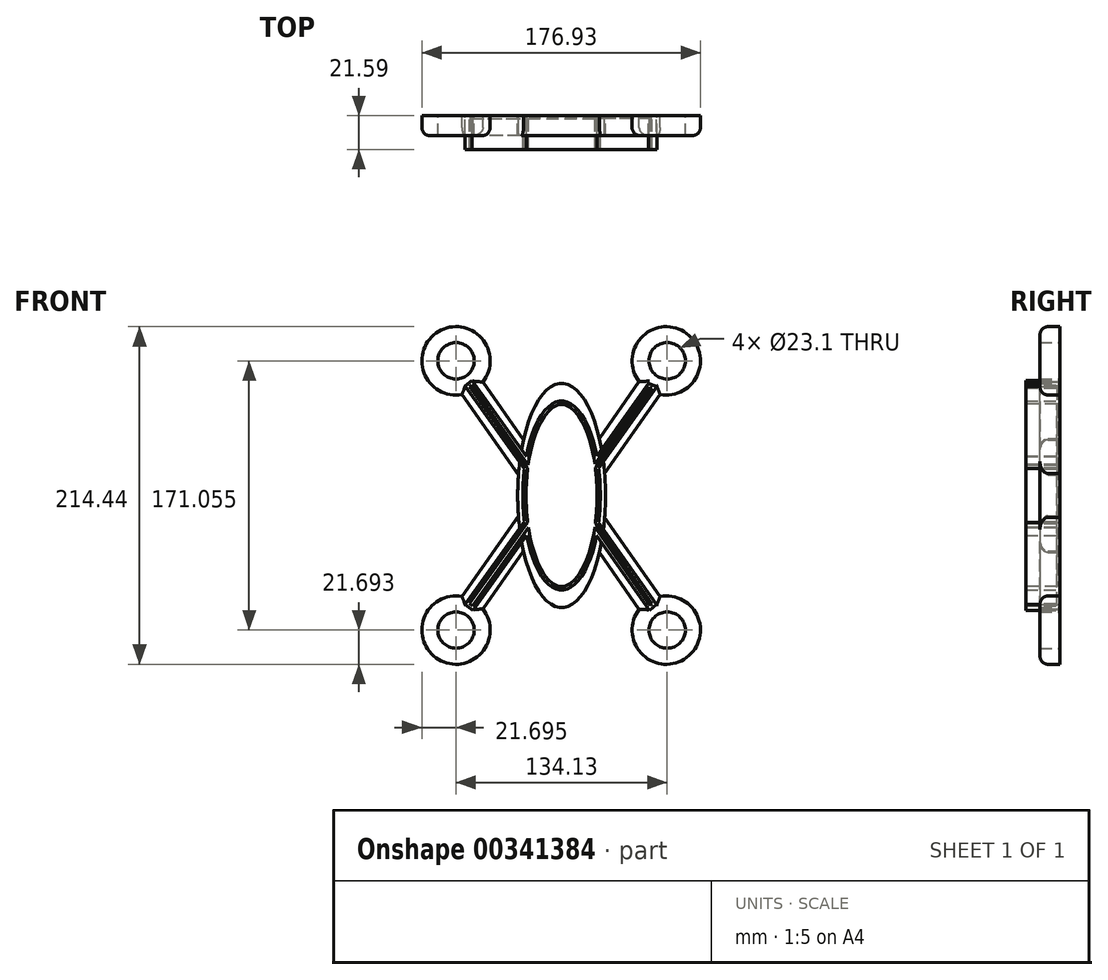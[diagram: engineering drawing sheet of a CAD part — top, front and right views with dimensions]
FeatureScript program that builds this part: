
annotation { "Feature Type Name" : "Feature", "Feature Type Description" : "" }
export const myFeature = defineFeature(function(context is Context, id is Id, definition is map)
    precondition{}
    {
        {
            var Q0;
            Q0=qCreatedBy(makeId("Front.planeOp"),FACE);
            var sketch = newSketch(context, id + "F0", { "sketchPlane" : qUnion([Q0])});
            skEllipse(sketch, "E0", {"center": v(0, 0) * mm, "majorRadius": 71.2 * mm, "minorRadius": 27.89 * mm, "majorAxis": v(0, -1)});
            skLineSegment(sketch, "E1.bottom", {"start": v(-14.74, 21.83) * mm, "end": v(-27.42, 12.95) * mm});
            skLineSegment(sketch, "E1.left", {"start": v(-14.74, 21.83) * mm, "end": v(-54.39, 78.44) * mm});
            skLineSegment(sketch, "E1.right", {"start": v(-27.42, 12.95) * mm, "end": v(-67.06, 69.56) * mm});
            skLineSegment(sketch, "E2.bottom", {"start": v(26.83, 13.26) * mm, "end": v(14.15, 22.14) * mm});
            skLineSegment(sketch, "E2.left", {"start": v(26.83, 13.26) * mm, "end": v(66.48, 69.87) * mm});
            skLineSegment(sketch, "E2.right", {"start": v(14.15, 22.14) * mm, "end": v(53.8, 78.75) * mm});
            skLineSegment(sketch, "E3", {"start": v(-14.74, 21.83) * mm, "end": v(0, 21.83) * mm});
            skLineSegment(sketch, "E4", {"start": v(0, 21.83) * mm, "end": v(14.15, 22.14) * mm});
            skLineSegment(sketch, "E5.MirrorCS", {"start": v(-14.74, -21.83) * mm, "end": v(-27.42, -12.95) * mm});
            skLineSegment(sketch, "E6.MirrorCS", {"start": v(-14.74, -21.83) * mm, "end": v(-54.39, -78.44) * mm});
            skLineSegment(sketch, "E7.MirrorCS", {"start": v(-27.42, -12.95) * mm, "end": v(-67.06, -69.56) * mm});
            skLineSegment(sketch, "E8.MirrorCS", {"start": v(-14.74, -21.83) * mm, "end": v(0, -21.83) * mm});
            skLineSegment(sketch, "E9.MirrorCS", {"start": v(0, -21.83) * mm, "end": v(14.15, -22.14) * mm});
            skLineSegment(sketch, "E10.MirrorCS", {"start": v(14.15, -22.14) * mm, "end": v(53.8, -78.75) * mm});
            skLineSegment(sketch, "E11.MirrorCS", {"start": v(26.83, -13.26) * mm, "end": v(66.48, -69.87) * mm});
            skLineSegment(sketch, "E12.MirrorCS", {"start": v(26.83, -13.26) * mm, "end": v(14.15, -22.14) * mm});
            skCircle(sketch, "E13", {"center": v(-67.06, 85.53) * mm, "radius": 21.7 * mm});
            skCircle(sketch, "E14", {"center": v(66.48, 85.53) * mm, "radius": 21.7 * mm});
            skCircle(sketch, "E15.MirrorC", {"center": v(-67.06, -85.53) * mm, "radius": 21.7 * mm});
            skCircle(sketch, "E16.MirrorC", {"center": v(66.48, -85.53) * mm, "radius": 21.7 * mm});
            skCircle(sketch, "E17", {"center": v(-67.06, 85.53) * mm, "radius": 11.55 * mm});
            skCircle(sketch, "E18.MirrorC", {"center": v(67.06, 85.53) * mm, "radius": 11.55 * mm});
            skCircle(sketch, "E19.MirrorC", {"center": v(-67.06, -85.53) * mm, "radius": 11.55 * mm});
            skCircle(sketch, "E20.MirrorC", {"center": v(67.06, -85.53) * mm, "radius": 11.55 * mm});
            skSolve(sketch);
        }
        {
            var Q0;
            Q0 = qSketchRegion(id + "F0", true);
            extrude(context, id + "F1", {"entities" : qUnion([Q0]), "depth" : 12.7 * mm});
        }
        {
            var Q0;
            Q0=makeQuery(id+"F1.opExtrude","CAP_EDGE",EDGE,{"disambiguationData":[OSD([sQuery(id+"F0.wireOp",EDGE,"E13")])],"isStart":false});
            var Q1;
            Q1=makeQuery(id+"F1.opExtrude","CAP_EDGE",EDGE,{"disambiguationData":[OSD([sQuery(id+"F0.wireOp",EDGE,"E14")])],"isStart":false});
            var Q2;
            Q2=makeQuery(id+"F1.opExtrude","CAP_EDGE",EDGE,{"disambiguationData":[OSD([sQuery(id+"F0.wireOp",EDGE,"E16.MirrorC")])],"isStart":false});
            var Q3;
            Q3=makeQuery(id+"F1.opExtrude","CAP_EDGE",EDGE,{"disambiguationData":[OSD([sQuery(id+"F0.wireOp",EDGE,"E15.MirrorC")])],"isStart":false});
            fillet(context, id + "F2", {"entities" : qUnion([Q0, Q1, Q2, Q3]), "radius" : 5.08 * mm, "tangentPropagation" : true, "allowEdgeOverflow" : false});
        }
        {
            var Q0;
            Q0=makeQuery(id+"F1.opExtrude","CAP_EDGE",EDGE,{"disambiguationData":[OSD([sQuery(id+"F0.wireOp",EDGE,"E1.right")])],"isStart":false});
            var Q1;
            Q1=makeQuery(id+"F1.opExtrude","CAP_EDGE",EDGE,{"disambiguationData":[OSD([sQuery(id+"F0.wireOp",EDGE,"E1.left")])],"isStart":false});
            var Q2;
            Q2=makeQuery(id+"F1.opExtrude","CAP_EDGE",EDGE,{"disambiguationData":[OSD([sQuery(id+"F0.wireOp",EDGE,"E2.right")])],"isStart":false});
            var Q3;
            Q3=makeQuery(id+"F1.opExtrude","CAP_EDGE",EDGE,{"disambiguationData":[OSD([sQuery(id+"F0.wireOp",EDGE,"E2.left")])],"isStart":false});
            var Q4;
            Q4=makeQuery(id+"F1.opExtrude","CAP_EDGE",EDGE,{"disambiguationData":[OSD([sQuery(id+"F0.wireOp",EDGE,"E11.MirrorCS")])],"isStart":false});
            var Q5;
            Q5=makeQuery(id+"F1.opExtrude","CAP_EDGE",EDGE,{"disambiguationData":[OSD([sQuery(id+"F0.wireOp",EDGE,"E10.MirrorCS")])],"isStart":false});
            var Q6;
            Q6=makeQuery(id+"F1.opExtrude","CAP_EDGE",EDGE,{"disambiguationData":[OSD([sQuery(id+"F0.wireOp",EDGE,"E6.MirrorCS")])],"isStart":false});
            var Q7;
            Q7=makeQuery(id+"F1.opExtrude","CAP_EDGE",EDGE,{"disambiguationData":[OSD([sQuery(id+"F0.wireOp",EDGE,"E7.MirrorCS")])],"isStart":false});
            fillet(context, id + "F3", {"entities" : qUnion([Q0, Q1, Q2, Q3, Q4, Q5, Q6, Q7]), "radius" : 5.08 * mm, "tangentPropagation" : true, "allowEdgeOverflow" : false});
        }
        {
            var Q0;
            Q0=qCreatedBy(makeId("Front.planeOp"),FACE);
            var sketch = newSketch(context, id + "F4", { "sketchPlane" : qUnion([Q0])});
            skEllipse(sketch, "E21", {"center": v(0, 0) * mm, "majorRadius": 59.97 * mm, "minorRadius": 24.6 * mm, "majorAxis": v(0, -1)});
            skLineSegment(sketch, "E22", {"start": v(-61.2, -69.14) * mm, "end": v(-23.64, -16.51) * mm});
            skLineSegment(sketch, "E23", {"start": v(-56.28, -72.98) * mm, "end": v(-22.28, -25.36) * mm});
            skLineSegment(sketch, "E24", {"start": v(-22.28, -25.36) * mm, "end": v(-23.64, -16.51) * mm});
            skLineSegment(sketch, "E25", {"start": v(-56.28, -72.98) * mm, "end": v(-61.2, -69.14) * mm});
            skLineSegment(sketch, "E26", {"start": v(55.93, -72.98) * mm, "end": v(22.28, -25.36) * mm});
            skLineSegment(sketch, "E27", {"start": v(60.27, -69.12) * mm, "end": v(23.56, -17.18) * mm});
            skLineSegment(sketch, "E28", {"start": v(-61.21, 69.6) * mm, "end": v(-23.6, 16.78) * mm});
            skLineSegment(sketch, "E29", {"start": v(-56.76, 72.95) * mm, "end": v(-22.4, 24.7) * mm});
            skLineSegment(sketch, "E30", {"start": v(-61.21, 69.6) * mm, "end": v(-56.76, 72.95) * mm});
            skLineSegment(sketch, "E31", {"start": v(55.11, 71.04) * mm, "end": v(60.5, 69.13) * mm});
            skLineSegment(sketch, "E32", {"start": v(55.93, -72.98) * mm, "end": v(60.27, -69.12) * mm});
            skLineSegment(sketch, "E33", {"start": v(60.5, 69.13) * mm, "end": v(23.55, 17.24) * mm});
            skLineSegment(sketch, "E34", {"start": v(55.11, 71.04) * mm, "end": v(22.34, 25.06) * mm});
            skSolve(sketch);
        }
        {
            var Q0;
            Q0 = qSketchRegion(id + "F4", true);
            extrude(context, id + "F5", {"entities" : qUnion([Q0]), "depth" : 21.59 * mm});
        }
        {
            var Q0;
            Q0=makeQuery(id+"F5.opExtrude","CAP_FACE",FACE,{"disambiguationData":[OSD([sQuery(id+"F4.wireOp",EDGE,"E21"),sQuery(id+"F4.wireOp",EDGE,"NEgBn6b3-1pjr-pe8X-6l68-krjNJmOewhNc"),sQuery(id+"F4.wireOp",EDGE,"9DAIEF9t-jXmu-CJTj-gN3L-F5fUEMQPX4Ks"),sQuery(id+"F4.wireOp",EDGE,"E22"),sQuery(id+"F4.wireOp",EDGE,"E23"),sQuery(id+"F4.wireOp",EDGE,"E25"),sQuery(id+"F4.wireOp",EDGE,"E26"),sQuery(id+"F4.wireOp",EDGE,"E27"),sQuery(id+"F4.wireOp",EDGE,"E28"),sQuery(id+"F4.wireOp",EDGE,"E29"),sQuery(id+"F4.wireOp",EDGE,"E30"),sQuery(id+"F4.wireOp",EDGE,"E31"),sQuery(id+"F4.wireOp",EDGE,"E32")])],"isStart":false});
            shell(context, id + "F6", {"entities" : qUnion([Q0]), "thickness" : 2.03 * mm});
        }
    });
